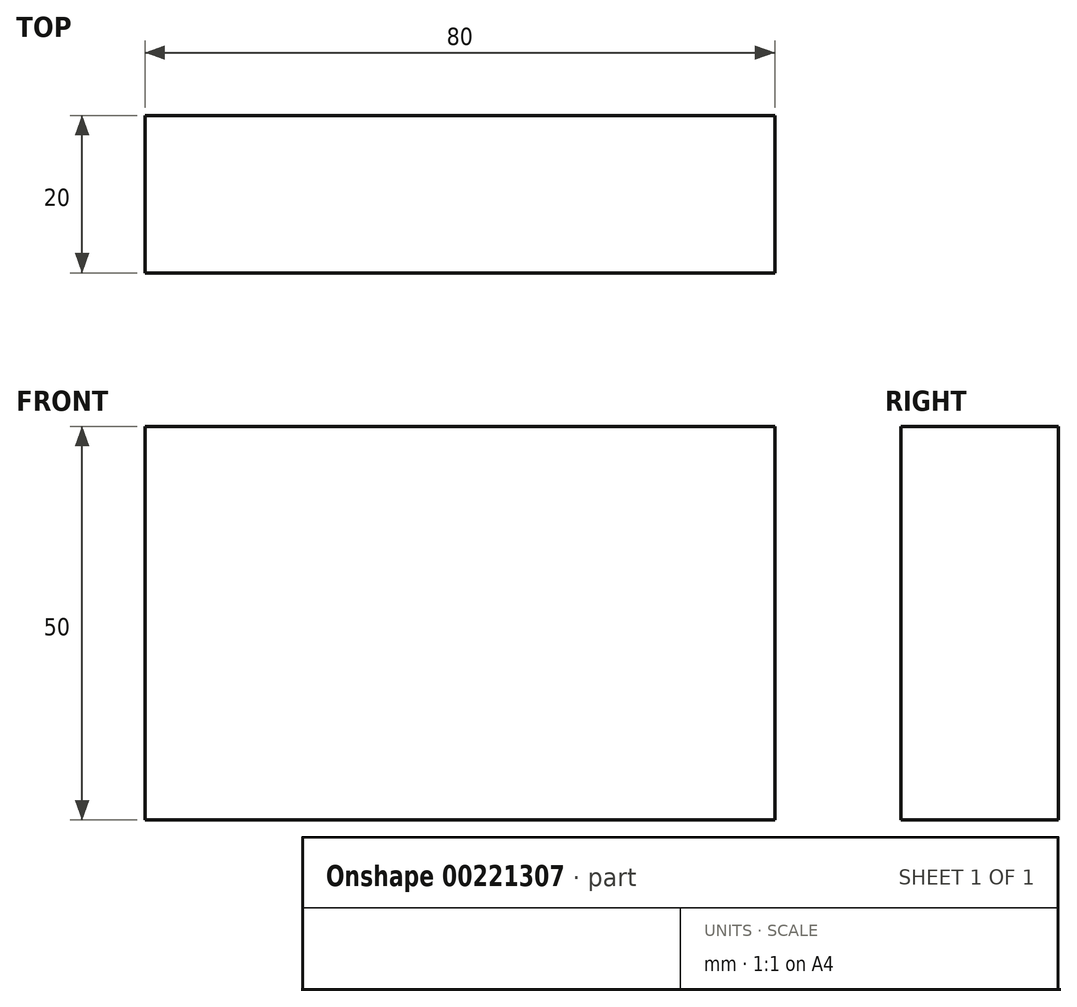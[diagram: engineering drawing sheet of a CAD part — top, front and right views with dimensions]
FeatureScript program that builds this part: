
annotation { "Feature Type Name" : "Feature", "Feature Type Description" : "" }
export const myFeature = defineFeature(function(context is Context, id is Id, definition is map)
    precondition{}
    {
        {
            var Q0;
            Q0=qCreatedBy(makeId("Front.planeOp"),FACE);
            var sketch = newSketch(context, id + "F0", { "sketchPlane" : qUnion([Q0])});
            skLineSegment(sketch, "E0.bottom", {"start": v(-23.91, 37.08) * mm, "end": v(56.09, 37.08) * mm});
            skLineSegment(sketch, "E0.top", {"start": v(-23.91, -12.92) * mm, "end": v(56.09, -12.92) * mm});
            skLineSegment(sketch, "E0.left", {"start": v(-23.91, 37.08) * mm, "end": v(-23.91, -12.92) * mm});
            skLineSegment(sketch, "E0.right", {"start": v(56.09, 37.08) * mm, "end": v(56.09, -12.92) * mm});
            skSolve(sketch);
        }
        {
            var Q0;
            Q0=makeQuery(id+"F0.imprint","IMPRINT",FACE,{"disambiguationData":[TD([[makeQuery(id+"F0.imprint","IMPRINT",EDGE,{"derivedFrom":sQuery(id+"F0.wireOp",EDGE,"E0.bottom")}),-1.0]])]});
            extrude(context, id + "F1", {"entities" : qUnion([Q0]), "oppositeDirection" : true, "depth" : 20 * mm});
        }
    });
